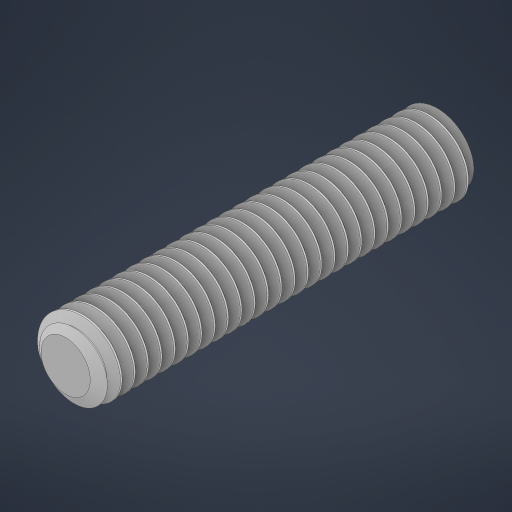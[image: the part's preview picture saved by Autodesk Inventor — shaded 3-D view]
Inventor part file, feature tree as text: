
AUTODESK INVENTOR PART (.ipt)
format: ipt  version: 2023 (Build 270158000, 158)  size: 999,424 bytes
history: native  units: in
note: dims shown in document units (in); Inventor stores cm internally (conversion verified against a paired STEP export)
features: mirror x1
ambient origin geometry x8: Origin, YZ Plane, XZ Plane, XY Plane, X Axis, Y Axis, Z Axis, Center Point
bodies: Solid1 (feature_tree)
feature tree (1):
  mirror  "Mirror1"
